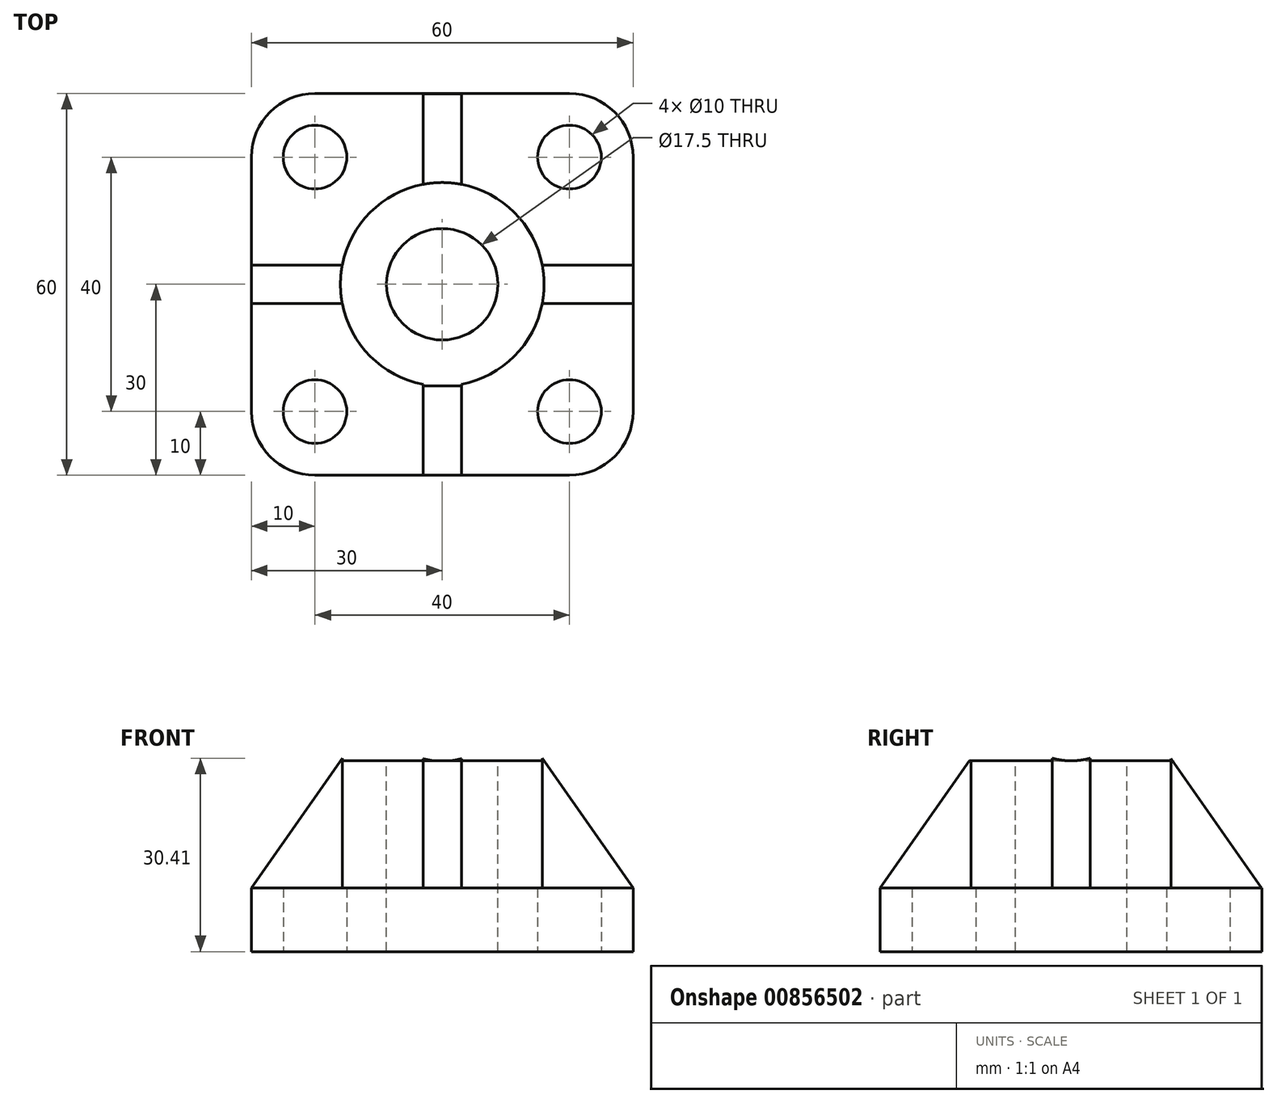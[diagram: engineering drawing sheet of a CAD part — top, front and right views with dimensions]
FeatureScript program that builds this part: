
annotation { "Feature Type Name" : "Feature", "Feature Type Description" : "" }
export const myFeature = defineFeature(function(context is Context, id is Id, definition is map)
    precondition{}
    {
        {
            var Q0;
            Q0=qCreatedBy(makeId("Top.planeOp"),FACE);
            var sketch = newSketch(context, id + "F0", { "sketchPlane" : qUnion([Q0])});
            skLineSegment(sketch, "E0.bottom", {"start": v(-30, -30) * mm, "end": v(30, -30) * mm});
            skLineSegment(sketch, "E0.top", {"start": v(-30, 30) * mm, "end": v(30, 30) * mm});
            skLineSegment(sketch, "E0.left", {"start": v(-30, -30) * mm, "end": v(-30, 30) * mm});
            skLineSegment(sketch, "E0.right", {"start": v(30, -30) * mm, "end": v(30, 30) * mm});
            skPoint(sketch, "E0.middle", {"position": v(0, 0) * mm});
            skLineSegment(sketch, "E1.bottom", {"start": v(-20, -20) * mm, "end": v(20, -20) * mm});
            skLineSegment(sketch, "E1.top", {"start": v(-20, 20) * mm, "end": v(20, 20) * mm});
            skLineSegment(sketch, "E1.left", {"start": v(-20, -20) * mm, "end": v(-20, 20) * mm});
            skLineSegment(sketch, "E1.right", {"start": v(20, -20) * mm, "end": v(20, 20) * mm});
            skPoint(sketch, "E2", {"position": v(-20, 20) * mm});
            skPoint(sketch, "E3", {"position": v(20, 20) * mm});
            skPoint(sketch, "E4", {"position": v(20, -20) * mm});
            skPoint(sketch, "E5", {"position": v(-20, -20) * mm});
            skSolve(sketch);
        }
        {
            var Q0;
            Q0=makeQuery(id+"F0.imprint","IMPRINT",FACE,{"disambiguationData":[TD([[makeQuery(id+"F0.imprint","IMPRINT",EDGE,{"derivedFrom":sQuery(id+"F0.wireOp",EDGE,"E0.bottom")}),1.0]])]});
            var Q1;
            Q1=makeQuery(id+"F0.imprint","IMPRINT",FACE,{"disambiguationData":[TD([[makeQuery(id+"F0.imprint","IMPRINT",EDGE,{"derivedFrom":sQuery(id+"F0.wireOp",EDGE,"E1.bottom")}),1.0]])]});
            extrude(context, id + "F1", {"entities" : qUnion([Q0, Q1]), "depth" : 10 * mm, "offsetDistance" : 25 * mm});
        }
        {
            var Q0;
            Q0=makeQuery(id+"F1.opExtrude","SWEPT_EDGE",EDGE,{"disambiguationData":[OSD([sQuery(id+"F0.wireOp",EDGE,"E0.top"),sQuery(id+"F0.wireOp",EDGE,"E0.left")])]});
            var Q1;
            Q1=makeQuery(id+"F1.opExtrude","SWEPT_EDGE",EDGE,{"disambiguationData":[OSD([sQuery(id+"F0.wireOp",EDGE,"E0.top"),sQuery(id+"F0.wireOp",EDGE,"E0.right")])]});
            var Q2;
            Q2=makeQuery(id+"F1.opExtrude","SWEPT_EDGE",EDGE,{"disambiguationData":[OSD([sQuery(id+"F0.wireOp",EDGE,"E0.bottom"),sQuery(id+"F0.wireOp",EDGE,"E0.right")])]});
            var Q3;
            Q3=makeQuery(id+"F1.opExtrude","SWEPT_EDGE",EDGE,{"disambiguationData":[OSD([sQuery(id+"F0.wireOp",EDGE,"E0.bottom"),sQuery(id+"F0.wireOp",EDGE,"E0.left")])]});
            fillet(context, id + "F2", {"entities" : qUnion([Q0, Q1, Q2, Q3]), "radius" : 10 * mm, "tangentPropagation" : true, "allowEdgeOverflow" : false});
        }
        {
            var Q0;
            Q0=sQuery(id+"F0.wireOp",VERTEX,"E2");
            var Q1;
            Q1=sQuery(id+"F0.wireOp",VERTEX,"E3");
            var Q2;
            Q2=sQuery(id+"F0.wireOp",VERTEX,"E4");
            var Q3;
            Q3=sQuery(id+"F0.wireOp",VERTEX,"E5");
            var Q4;
            Q4=makeQuery(id+"F1.opExtrude","SWEPT_BODY",BODY,{"disambiguationData":[OSD([sQuery(id+"F0.wireOp",EDGE,"E0.bottom"),sQuery(id+"F0.wireOp",EDGE,"E0.top"),sQuery(id+"F0.wireOp",EDGE,"E0.left"),sQuery(id+"F0.wireOp",EDGE,"E0.right")])]});
            hole(context, id + "F3", {"style" : HoleStyle.SIMPLE, "endStyle" : HoleEndStyle.BLIND, "oppositeDirection" : true, "holeDiameter" : 10 * mm, "majorDiameter" : 16 * mm, "holeDepth" : 10 * mm, "isTappedThrough" : true, "tappedDepth" : 12 * mm, "tapClearance" : 3, "locations" : qUnion([Q0, Q1, Q2, Q3]), "scope" : qUnion([Q4])});
        }
        {
            var Q0;
            Q0=makeQuery(id+"F1.opExtrude","CAP_FACE",FACE,{"disambiguationData":[OSD([sQuery(id+"F0.wireOp",EDGE,"E0.bottom"),sQuery(id+"F0.wireOp",EDGE,"E0.top"),sQuery(id+"F0.wireOp",EDGE,"E0.left"),sQuery(id+"F0.wireOp",EDGE,"E0.right")])],"isStart":false});
            var sketch = newSketch(context, id + "F4", { "sketchPlane" : qUnion([Q0])});
            skCircle(sketch, "E6", {"center": v(0, 0) * mm, "radius": 16 * mm});
            skSolve(sketch);
        }
        {
            var Q0;
            Q0=qCreatedBy(makeId("Front.planeOp"),FACE);
            var sketch = newSketch(context, id + "F5", { "sketchPlane" : qUnion([Q0])});
            skLineSegment(sketch, "E7", {"start": v(0, 0) * mm, "end": v(-2, 0) * mm});
            skLineSegment(sketch, "E8", {"start": v(-2, 0) * mm, "end": v(-2, 10) * mm});
            skLineSegment(sketch, "E9", {"start": v(-2, 10) * mm, "end": v(-30, 10) * mm});
            skLineSegment(sketch, "E10", {"start": v(-30, 10) * mm, "end": v(-2, 50) * mm});
            skLineSegment(sketch, "E11", {"start": v(-2, 50) * mm, "end": v(-2, 10) * mm});
            skLineSegment(sketch, "E12", {"start": v(-2, 10) * mm, "end": v(2, 10) * mm});
            skLineSegment(sketch, "E13", {"start": v(2, 10) * mm, "end": v(2, 50) * mm});
            skLineSegment(sketch, "E14", {"start": v(2, 10) * mm, "end": v(30, 10) * mm});
            skLineSegment(sketch, "E15", {"start": v(30, 10) * mm, "end": v(2, 50) * mm});
            skSolve(sketch);
        }
        {
            var Q0;
            Q0=makeQuery(id+"F5.imprint","IMPRINT",FACE,{"disambiguationData":[TD([[makeQuery(id+"F5.imprint","IMPRINT",EDGE,{"derivedFrom":sQuery(id+"F5.wireOp",EDGE,"E9")}),-1.0]])]});
            var Q1;
            Q1=makeQuery(id+"F5.imprint","IMPRINT",FACE,{"disambiguationData":[TD([[makeQuery(id+"F5.imprint","IMPRINT",EDGE,{"derivedFrom":sQuery(id+"F5.wireOp",EDGE,"E13")}),-1.0]])]});
            extrude(context, id + "F6", {"entities" : qUnion([Q0, Q1]), "operationType" : NewBodyOperationType.ADD, "endBound" : BoundingType.SYMMETRIC, "depth" : 6 * mm, "offsetDistance" : 25 * mm});
        }
        {
            var Q0;
            Q0=makeQuery(id+"F4.imprint","IMPRINT",FACE,{"disambiguationData":[TD([[makeQuery(id+"F4.imprint","IMPRINT",EDGE,{"derivedFrom":sQuery(id+"F4.wireOp",EDGE,"E6")}),1.0]])]});
            extrude(context, id + "F7", {"entities" : qUnion([Q0]), "operationType" : NewBodyOperationType.REMOVE, "oppositeDirection" : true, "depth" : -40 * mm, "offsetDistance" : 25 * mm});
        }
        {
            var Q0;
            Q0=qCreatedBy(makeId("Right.planeOp"),FACE);
            var sketch = newSketch(context, id + "F8", { "sketchPlane" : qUnion([Q0])});
            skLineSegment(sketch, "E16", {"start": v(0, 0) * mm, "end": v(2, 0) * mm});
            skLineSegment(sketch, "E17", {"start": v(2, 0) * mm, "end": v(30, 0) * mm});
            skLineSegment(sketch, "E18", {"start": v(0, 0) * mm, "end": v(-2, 0) * mm});
            skLineSegment(sketch, "E19", {"start": v(-2, 0) * mm, "end": v(-30, 0) * mm});
            skLineSegment(sketch, "E20", {"start": v(30, 0) * mm, "end": v(30, 9.93) * mm});
            skLineSegment(sketch, "E21", {"start": v(-30, 0) * mm, "end": v(-30, 10) * mm});
            skLineSegment(sketch, "E22", {"start": v(30, 9.93) * mm, "end": v(2, 9.93) * mm});
            skLineSegment(sketch, "E23", {"start": v(-30, 10) * mm, "end": v(-2, 10) * mm});
            skLineSegment(sketch, "E24", {"start": v(2, 9.93) * mm, "end": v(2, 49.93) * mm});
            skLineSegment(sketch, "E25", {"start": v(-2, 10) * mm, "end": v(-2, 50) * mm});
            skLineSegment(sketch, "E26", {"start": v(2, 49.93) * mm, "end": v(30, 9.93) * mm});
            skLineSegment(sketch, "E27", {"start": v(-2, 50) * mm, "end": v(-30, 10) * mm});
            skSolve(sketch);
        }
        {
            var Q0;
            Q0=makeQuery(id+"F8.imprint","IMPRINT",FACE,{"disambiguationData":[TD([[makeQuery(id+"F8.imprint","IMPRINT",EDGE,{"derivedFrom":sQuery(id+"F8.wireOp",EDGE,"E22")}),-1.0]])]});
            var Q1;
            Q1=makeQuery(id+"F8.imprint","IMPRINT",FACE,{"disambiguationData":[TD([[makeQuery(id+"F8.imprint","IMPRINT",EDGE,{"derivedFrom":sQuery(id+"F8.wireOp",EDGE,"E23")}),1.0]])]});
            extrude(context, id + "F9", {"entities" : qUnion([Q0, Q1]), "operationType" : NewBodyOperationType.ADD, "endBound" : BoundingType.SYMMETRIC, "depth" : 6 * mm, "offsetDistance" : 25 * mm});
        }
        {
            var Q0;
            Q0=makeQuery(id+"F4.imprint","IMPRINT",FACE,{"disambiguationData":[TD([[makeQuery(id+"F4.imprint","IMPRINT",EDGE,{"derivedFrom":sQuery(id+"F4.wireOp",EDGE,"E6")}),1.0]])]});
            extrude(context, id + "F10", {"entities" : qUnion([Q0]), "operationType" : NewBodyOperationType.REMOVE, "oppositeDirection" : true, "depth" : -40 * mm, "offsetDistance" : 25 * mm});
        }
        {
            var Q0;
            Q0=makeQuery(id+"F4.imprint","IMPRINT",FACE,{"disambiguationData":[TD([[makeQuery(id+"F4.imprint","IMPRINT",EDGE,{"derivedFrom":sQuery(id+"F4.wireOp",EDGE,"E6")}),1.0]])]});
            extrude(context, id + "F11", {"entities" : qUnion([Q0]), "operationType" : NewBodyOperationType.ADD, "depth" : 20 * mm, "offsetDistance" : 25 * mm});
        }
        {
            var Q0;
            Q0=makeQuery(id+"F11.opExtrude","CAP_FACE",FACE,{"disambiguationData":[OSD([sQuery(id+"F4.wireOp",EDGE,"E6")])],"isStart":false});
            var sketch = newSketch(context, id + "F12", { "sketchPlane" : qUnion([Q0])});
            skPoint(sketch, "E28", {"position": v(0, 0) * mm});
            skSolve(sketch);
        }
        {
            var Q0;
            Q0=sQuery(id+"F12.wireOp",VERTEX,"E28");
            var Q1;
            Q1=makeQuery(id+"F1.opExtrude","SWEPT_BODY",BODY,{"disambiguationData":[OSD([sQuery(id+"F0.wireOp",EDGE,"E0.bottom"),sQuery(id+"F0.wireOp",EDGE,"E0.top"),sQuery(id+"F0.wireOp",EDGE,"E0.left"),sQuery(id+"F0.wireOp",EDGE,"E0.right")])]});
            hole(context, id + "F13", {"style" : HoleStyle.SIMPLE, "endStyle" : HoleEndStyle.BLIND, "standardTappedOrClearance" : lookupTablePath({ "fit" : "Normal", "standard" : "ISO", "size" : "M16", "type" : "Clearance" }), "standardBlindInLast" : lookupTablePath({ "fit" : "Standard", "standard" : "ISO", "size" : "M16", "type" : "Clearance" }), "holeDiameter" : 17.5 * mm, "majorDiameter" : 5 * mm, "holeDepth" : 30 * mm, "isTappedThrough" : true, "tappedDepth" : 12 * mm, "tapClearance" : 3, "locations" : qUnion([Q0]), "scope" : qUnion([Q1])});
        }
        {
            var Q0;
            Q0=makeQuery(id+"F9.opExtrude","CAP_FACE",FACE,{"disambiguationData":[OSD([sQuery(id+"F8.wireOp",EDGE,"E23"),sQuery(id+"F8.wireOp",EDGE,"E25"),sQuery(id+"F8.wireOp",EDGE,"E27")])],"isStart":false});
            var sketch = newSketch(context, id + "F14", { "sketchPlane" : qUnion([Q0])});
            skLineSegment(sketch, "E29", {"start": v(-15.72, 30) * mm, "end": v(-16, 30) * mm});
            skSolve(sketch);
        }
        {
            var Q0;
            {var subQ0=sQuery(id+"F14.wireOp",EDGE,"E29");Q0=makeQuery(id+"F14.imprint","IMPRINT",FACE,{"disambiguationData":[TD([[makeQuery(id+"F14.imprint","IMPRINT",EDGE,{"derivedFrom":subQ0}),-1.0]])]});}
            extrude(context, id + "F15", {"entities" : qUnion([Q0]), "operationType" : NewBodyOperationType.REMOVE, "oppositeDirection" : true, "depth" : 25 * mm, "offsetDistance" : 25 * mm});
        }
    });
